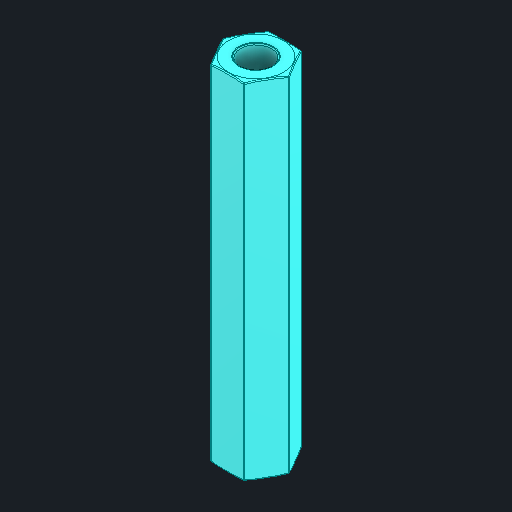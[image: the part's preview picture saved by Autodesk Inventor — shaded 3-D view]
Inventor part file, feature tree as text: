
AUTODESK INVENTOR PART (.ipt)
format: ipt  version: 2025 (Build 290162000, 162)  size: 168,448 bytes
history: native  units: in
note: dims shown in document units (in); Inventor stores cm internally (conversion verified against a paired STEP export)
features: fillet x1
ambient origin geometry x8: Origin, YZ Plane, XZ Plane, XY Plane, X Axis, Y Axis, Z Axis, Center Point
bodies: Solid1 (feature_tree)
feature tree (1):
  fillet  "Fillet1"  [1 undecoded]
note: 1 required parameter value undecoded (feature->parameter linkage not recoverable at this tier; creation-order binding heuristic only, values carry confidence <= 0.55)
